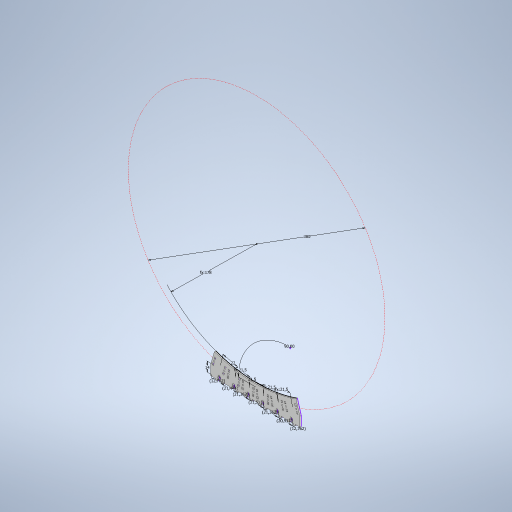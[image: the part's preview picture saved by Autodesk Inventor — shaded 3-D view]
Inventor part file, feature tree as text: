
AUTODESK INVENTOR PART (.ipt)
format: ipt  version: 2024.1 (Build 281209000, 209)  size: 2,059,776 bytes
history: native  units: mm
features: other x25, extrude x4, sketch x3
ambient origin geometry x8: Origin, YZ Plane, XZ Plane, XY Plane, X Axis, Y Axis, Z Axis, Center Point
bodies: Body1 (feature_tree)
feature tree (32):
  other  "Table"
  other  "shared_parameters.ipt"
  other  "keywell_support-back"
  other  "keywell_support-front"
  other  "keywell_support-front-r6"
  other  "Blocs"
  extrude  "Base"  Depth=2.0mm TaperAngle=0.0deg
  extrude  "Front: substract"  Depth=178.0mm
  extrude  "Front r6: substract"  Depth=1.5mm TaperAngle=0.0deg
  extrude  "Gain de place"  TaperAngle=0.0deg  [1 undecoded]
  sketch  "Esquisse5"
  sketch  "Esquisse7"
  other  "Anchor (screw side)"
  other  "Anchor (nut side)"
  other  "Screwless anchor (male)"
  other  "Screwless anchor (female)"
  other  "Anchor"
  sketch  "Esquisse9"
  other  "Anchor (screw side):3"
  other  "Anchor (screw side):4"
  other  "Anchor:1"
  other  "Anchor:2"
  other  "Anchor:3"
  other  "Anchor:4"
  other  "Anchor:5"
  other  "Anchor:6"
  other  "Anchor (nut side):1"
  other  "Anchor (nut side):2"
  other  "Anchor (nut side):3"
  other  "Anchor (nut side):4"
  other  "Anchor (nut side):5"
  other  "Anchor (nut side):6"
note: 1 required parameter value undecoded (feature->parameter linkage not recoverable at this tier; creation-order binding heuristic only, values carry confidence <= 0.55)
